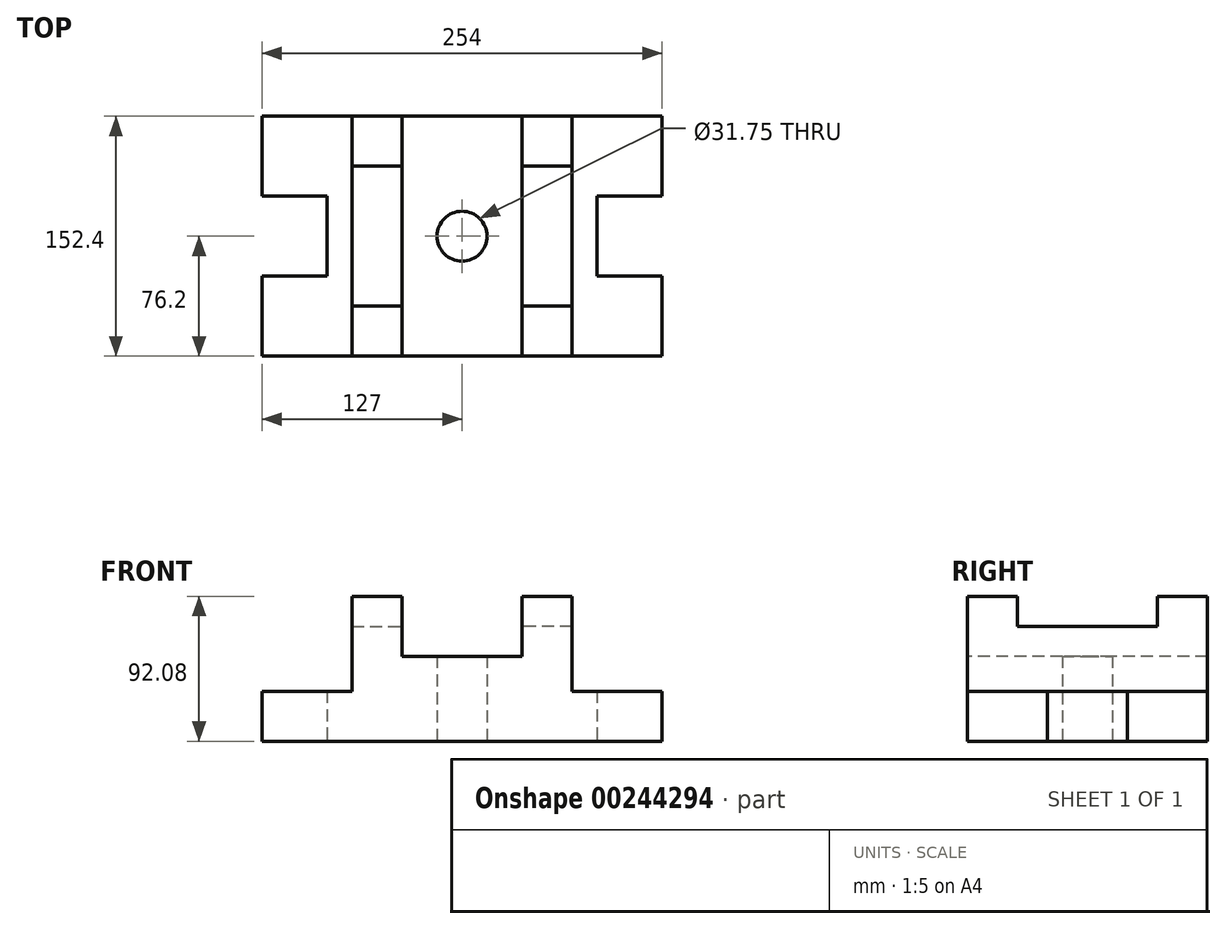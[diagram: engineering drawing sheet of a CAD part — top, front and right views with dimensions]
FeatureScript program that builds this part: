
annotation { "Feature Type Name" : "Feature", "Feature Type Description" : "" }
export const myFeature = defineFeature(function(context is Context, id is Id, definition is map)
    precondition{}
    {
        {
            var Q0;
            Q0=qCreatedBy(makeId("Top.planeOp"),FACE);
            var sketch = newSketch(context, id + "F0", { "sketchPlane" : qUnion([Q0])});
            skCircle(sketch, "E0", {"center": v(0, 0) * mm, "radius": 15.88 * mm});
            skLineSegment(sketch, "E1", {"start": v(0, 0) * mm, "end": v(0, 76.2) * mm});
            skLineSegment(sketch, "E2", {"start": v(0, 0) * mm, "end": v(0, -76.2) * mm});
            skLineSegment(sketch, "E3", {"start": v(0, -76.2) * mm, "end": v(38.1, -76.2) * mm});
            skLineSegment(sketch, "E4", {"start": v(0, 76.2) * mm, "end": v(38.1, 76.2) * mm});
            skLineSegment(sketch, "E5", {"start": v(38.1, 76.2) * mm, "end": v(69.85, 76.2) * mm});
            skLineSegment(sketch, "E6", {"start": v(38.1, -76.2) * mm, "end": v(69.85, -76.2) * mm});
            skLineSegment(sketch, "E7", {"start": v(69.85, 76.2) * mm, "end": v(127, 76.2) * mm});
            skLineSegment(sketch, "E8", {"start": v(69.85, -76.2) * mm, "end": v(127, -76.2) * mm});
            skLineSegment(sketch, "E9", {"start": v(38.1, 76.2) * mm, "end": v(38.1, -76.2) * mm});
            skLineSegment(sketch, "E10", {"start": v(69.85, 76.2) * mm, "end": v(69.85, -76.2) * mm});
            skLineSegment(sketch, "E11", {"start": v(127, -76.2) * mm, "end": v(127, -25.4) * mm});
            skLineSegment(sketch, "E12", {"start": v(127, 76.2) * mm, "end": v(127, 25.4) * mm});
            skLineSegment(sketch, "E13", {"start": v(127, 25.4) * mm, "end": v(85.72, 25.4) * mm});
            skLineSegment(sketch, "E14", {"start": v(127, -25.4) * mm, "end": v(85.72, -25.4) * mm});
            skLineSegment(sketch, "E15", {"start": v(85.72, 25.4) * mm, "end": v(85.72, -25.4) * mm});
            skLineSegment(sketch, "E16.MirrorCS", {"start": v(-38.1, 76.2) * mm, "end": v(-38.1, -76.2) * mm});
            skLineSegment(sketch, "E17.MirrorCS", {"start": v(0, -76.2) * mm, "end": v(-38.1, -76.2) * mm});
            skLineSegment(sketch, "E18.MirrorCS", {"start": v(-38.1, -76.2) * mm, "end": v(-69.85, -76.2) * mm});
            skLineSegment(sketch, "E19.MirrorCS", {"start": v(-69.85, -76.2) * mm, "end": v(-127, -76.2) * mm});
            skLineSegment(sketch, "E20.MirrorCS", {"start": v(-127, -76.2) * mm, "end": v(-127, -25.4) * mm});
            skLineSegment(sketch, "E21.MirrorCS", {"start": v(-127, -25.4) * mm, "end": v(-85.72, -25.4) * mm});
            skLineSegment(sketch, "E22.MirrorCS", {"start": v(-85.72, 25.4) * mm, "end": v(-85.72, -25.4) * mm});
            skLineSegment(sketch, "E23.MirrorCS", {"start": v(-127, 25.4) * mm, "end": v(-85.72, 25.4) * mm});
            skLineSegment(sketch, "E24.MirrorCS", {"start": v(-127, 76.2) * mm, "end": v(-127, 25.4) * mm});
            skLineSegment(sketch, "E25.MirrorCS", {"start": v(-69.85, 76.2) * mm, "end": v(-127, 76.2) * mm});
            skLineSegment(sketch, "E26.MirrorCS", {"start": v(-38.1, 76.2) * mm, "end": v(-69.85, 76.2) * mm});
            skLineSegment(sketch, "E27.MirrorCS", {"start": v(0, 76.2) * mm, "end": v(-38.1, 76.2) * mm});
            skLineSegment(sketch, "E28.MirrorCS", {"start": v(-69.85, 76.2) * mm, "end": v(-69.85, -76.2) * mm});
            skLineSegment(sketch, "E29", {"start": v(69.85, -76.2) * mm, "end": v(69.85, -44.45) * mm});
            skLineSegment(sketch, "E30", {"start": v(69.85, -44.45) * mm, "end": v(38.1, -44.45) * mm});
            skLineSegment(sketch, "E31.MirrorCS", {"start": v(69.85, 44.45) * mm, "end": v(38.1, 44.45) * mm});
            skLineSegment(sketch, "E32.MirrorCS", {"start": v(-69.85, 44.45) * mm, "end": v(-38.1, 44.45) * mm});
            skLineSegment(sketch, "E33.MirrorCS", {"start": v(-69.85, -44.45) * mm, "end": v(-38.1, -44.45) * mm});
            skSolve(sketch);
        }
        {
            var Q0;
            {var subQ1=sQuery(id+"F0.wireOp",EDGE,"E19.MirrorCS");Q0=makeQuery(id+"F0.imprint","IMPRINT",FACE,{"disambiguationData":[TD([[makeQuery(id+"F0.imprint","IMPRINT",EDGE,{"derivedFrom":subQ1}),-1.0]])]});}
            var Q1;
            {var subQ3=sQuery(id+"F0.wireOp",EDGE,"E7");Q1=makeQuery(id+"F0.imprint","IMPRINT",FACE,{"disambiguationData":[TD([[makeQuery(id+"F0.imprint","IMPRINT",EDGE,{"derivedFrom":subQ3}),-1.0]])]});}
            extrude(context, id + "F1", {"entities" : qUnion([Q0, Q1]), "depth" : 31.75 * mm});
        }
        {
            var Q0;
            {var subQ0=sQuery(id+"F0.wireOp",EDGE,"E17.MirrorCS");Q0=makeQuery(id+"F0.imprint","IMPRINT",FACE,{"disambiguationData":[TD([[makeQuery(id+"F0.imprint","IMPRINT",EDGE,{"derivedFrom":subQ0}),-1.0]])]});}
            var Q1;
            {var subQ6=sQuery(id+"F0.wireOp",EDGE,"E3");Q1=makeQuery(id+"F0.imprint","IMPRINT",FACE,{"disambiguationData":[TD([[makeQuery(id+"F0.imprint","IMPRINT",EDGE,{"derivedFrom":subQ6}),1.0]])]});}
            extrude(context, id + "F2", {"entities" : qUnion([Q0, Q1]), "operationType" : NewBodyOperationType.ADD, "depth" : 53.97 * mm});
        }
        {
            var Q0;
            {var subQ0=sQuery(id+"F0.wireOp",EDGE,"E26.MirrorCS");Q0=makeQuery(id+"F0.imprint","IMPRINT",FACE,{"disambiguationData":[TD([[makeQuery(id+"F0.imprint","IMPRINT",EDGE,{"derivedFrom":subQ0}),1.0]])]});}
            var Q1;
            {var subQ0=sQuery(id+"F0.wireOp",EDGE,"E18.MirrorCS");Q1=makeQuery(id+"F0.imprint","IMPRINT",FACE,{"disambiguationData":[TD([[makeQuery(id+"F0.imprint","IMPRINT",EDGE,{"derivedFrom":subQ0}),-1.0]])]});}
            var Q2;
            {var subQ0=sQuery(id+"F0.wireOp",EDGE,"E5");Q2=makeQuery(id+"F0.imprint","IMPRINT",FACE,{"disambiguationData":[TD([[makeQuery(id+"F0.imprint","IMPRINT",EDGE,{"derivedFrom":subQ0}),-1.0]])]});}
            var Q3;
            {var subQ0=sQuery(id+"F0.wireOp",EDGE,"E6");Q3=makeQuery(id+"F0.imprint","IMPRINT",FACE,{"disambiguationData":[TD([[makeQuery(id+"F0.imprint","IMPRINT",EDGE,{"derivedFrom":subQ0}),1.0]])]});}
            extrude(context, id + "F3", {"entities" : qUnion([Q0, Q1, Q2, Q3]), "operationType" : NewBodyOperationType.ADD, "depth" : 92.07 * mm});
        }
        {
            var Q0;
            {var subQ0=sQuery(id+"F0.wireOp",EDGE,"E30");Q0=makeQuery(id+"F0.imprint","IMPRINT",FACE,{"disambiguationData":[TD([[makeQuery(id+"F0.imprint","IMPRINT",EDGE,{"derivedFrom":subQ0}),-1.0]])]});}
            var Q1;
            {var subQ0=sQuery(id+"F0.wireOp",EDGE,"E32.MirrorCS");Q1=makeQuery(id+"F0.imprint","IMPRINT",FACE,{"disambiguationData":[TD([[makeQuery(id+"F0.imprint","IMPRINT",EDGE,{"derivedFrom":subQ0}),-1.0]])]});}
            extrude(context, id + "F4", {"entities" : qUnion([Q0, Q1]), "operationType" : NewBodyOperationType.ADD, "depth" : 73.02 * mm});
        }
    });
